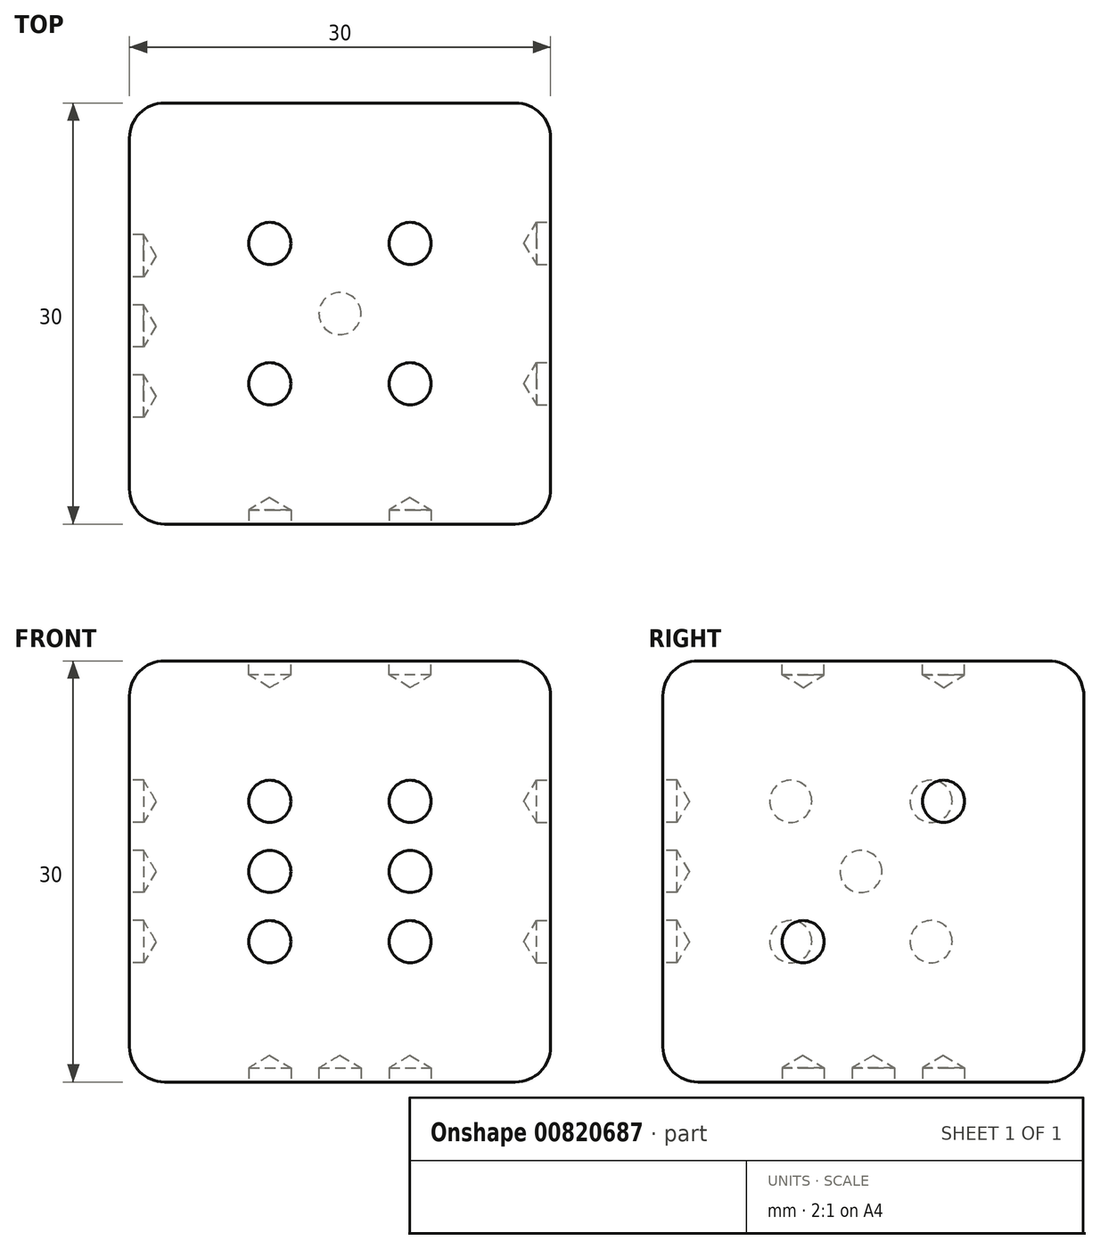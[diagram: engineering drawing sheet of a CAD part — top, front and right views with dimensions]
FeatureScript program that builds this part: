
annotation { "Feature Type Name" : "Feature", "Feature Type Description" : "" }
export const myFeature = defineFeature(function(context is Context, id is Id, definition is map)
    precondition{}
    {
        {
            var Q0;
            Q0=qCreatedBy(makeId("Front.planeOp"),FACE);
            var sketch = newSketch(context, id + "F0", { "sketchPlane" : qUnion([Q0])});
            skLineSegment(sketch, "E0.bottom", {"start": v(15, 15) * mm, "end": v(-15, 15) * mm});
            skLineSegment(sketch, "E0.top", {"start": v(15, -15) * mm, "end": v(-15, -15) * mm});
            skLineSegment(sketch, "E0.left", {"start": v(15, 15) * mm, "end": v(15, -15) * mm});
            skLineSegment(sketch, "E0.right", {"start": v(-15, 15) * mm, "end": v(-15, -15) * mm});
            skPoint(sketch, "E0.middle", {"position": v(0, 0) * mm});
            skSolve(sketch);
        }
        {
            var Q0;
            Q0 = qSketchRegion(id + "F0", true);
            extrude(context, id + "F1", {"entities" : qUnion([Q0]), "depth" : 30 * mm, "offsetDistance" : 25.4 * mm});
        }
        {
            var Q0;
            Q0=makeQuery(id+"F1.opExtrude","CAP_FACE",FACE,{"disambiguationData":[OSD([sQuery(id+"F0.wireOp",EDGE,"E0.bottom"),sQuery(id+"F0.wireOp",EDGE,"E0.top"),sQuery(id+"F0.wireOp",EDGE,"E0.left"),sQuery(id+"F0.wireOp",EDGE,"E0.right")])],"isStart":false});
            var Q1;
            Q1=makeQuery(id+"F1.opExtrude","SWEPT_FACE",FACE,{"disambiguationData":[OSD([sQuery(id+"F0.wireOp",EDGE,"E0.bottom")])]});
            var Q2;
            Q2=makeQuery(id+"F1.opExtrude","SWEPT_FACE",FACE,{"disambiguationData":[OSD([sQuery(id+"F0.wireOp",EDGE,"E0.left")])]});
            var Q3;
            Q3=makeQuery(id+"F1.opExtrude","SWEPT_FACE",FACE,{"disambiguationData":[OSD([sQuery(id+"F0.wireOp",EDGE,"E0.right")])]});
            var Q4;
            Q4=makeQuery(id+"F1.opExtrude","SWEPT_FACE",FACE,{"disambiguationData":[OSD([sQuery(id+"F0.wireOp",EDGE,"E0.top")])]});
            var Q5;
            Q5=makeQuery(id+"F1.opExtrude","CAP_FACE",FACE,{"disambiguationData":[OSD([sQuery(id+"F0.wireOp",EDGE,"E0.bottom"),sQuery(id+"F0.wireOp",EDGE,"E0.top"),sQuery(id+"F0.wireOp",EDGE,"E0.left"),sQuery(id+"F0.wireOp",EDGE,"E0.right")])],"isStart":true});
            fillet(context, id + "F2", {"entities" : qUnion([Q0, Q1, Q2, Q3, Q4, Q5]), "radius" : 2.5 * mm, "tangentPropagation" : true, "allowEdgeOverflow" : false});
        }
        {
            var Q0;
            Q0=makeQuery(id+"F1.opExtrude","CAP_FACE",FACE,{"disambiguationData":[OSD([sQuery(id+"F0.wireOp",EDGE,"E0.bottom"),sQuery(id+"F0.wireOp",EDGE,"E0.top"),sQuery(id+"F0.wireOp",EDGE,"E0.left"),sQuery(id+"F0.wireOp",EDGE,"E0.right")])],"isStart":false});
            var sketch = newSketch(context, id + "F3", { "sketchPlane" : qUnion([Q0])});
            skPoint(sketch, "E1.middle", {"position": v(0, 0) * mm});
            skPoint(sketch, "E2", {"position": v(-5, 0) * mm});
            skPoint(sketch, "E3", {"position": v(-5, 5) * mm});
            skPoint(sketch, "E4", {"position": v(-5, -5) * mm});
            skPoint(sketch, "E5", {"position": v(5, -5) * mm});
            skPoint(sketch, "E6", {"position": v(5, 5) * mm});
            skPoint(sketch, "E7", {"position": v(5, 0) * mm});
            skSolve(sketch);
        }
        {
            var Q0;
            Q0=makeQuery(id+"F1.opExtrude","SWEPT_FACE",FACE,{"disambiguationData":[OSD([sQuery(id+"F0.wireOp",EDGE,"E0.bottom")])]});
            var sketch = newSketch(context, id + "F4", { "sketchPlane" : qUnion([Q0])});
            skPoint(sketch, "E8.middle", {"position": v(0, 0) * mm});
            skPoint(sketch, "E9", {"position": v(-5, -10) * mm});
            skPoint(sketch, "E10", {"position": v(5, -10) * mm});
            skPoint(sketch, "E11", {"position": v(5, -20) * mm});
            skPoint(sketch, "E12", {"position": v(-5, -20) * mm});
            skSolve(sketch);
        }
        {
            var Q0;
            Q0=makeQuery(id+"F1.opExtrude","SWEPT_FACE",FACE,{"disambiguationData":[OSD([sQuery(id+"F0.wireOp",EDGE,"E0.top")])]});
            var sketch = newSketch(context, id + "F5", { "sketchPlane" : qUnion([Q0])});
            skPoint(sketch, "E13.middle", {"position": v(0, 0) * mm});
            skPoint(sketch, "E14", {"position": v(0, 15) * mm});
            skPoint(sketch, "E15", {"position": v(-5, 10) * mm});
            skPoint(sketch, "E16", {"position": v(5, 20) * mm});
            skSolve(sketch);
        }
        {
            var Q0;
            Q0=makeQuery(id+"F1.opExtrude","SWEPT_FACE",FACE,{"disambiguationData":[OSD([sQuery(id+"F0.wireOp",EDGE,"E0.right")])]});
            var sketch = newSketch(context, id + "F6", { "sketchPlane" : qUnion([Q0])});
            skPoint(sketch, "E17.middle", {"position": v(0.88, 0) * mm});
            skPoint(sketch, "E18", {"position": v(15.88, 0) * mm});
            skPoint(sketch, "E19", {"position": v(10.88, 5) * mm});
            skPoint(sketch, "E20", {"position": v(20.88, 5) * mm});
            skPoint(sketch, "E21", {"position": v(20.88, -5) * mm});
            skPoint(sketch, "E22", {"position": v(10.88, -5) * mm});
            skSolve(sketch);
        }
        {
            var Q0;
            Q0=makeQuery(id+"F1.opExtrude","SWEPT_FACE",FACE,{"disambiguationData":[OSD([sQuery(id+"F0.wireOp",EDGE,"E0.left")])]});
            var sketch = newSketch(context, id + "F7", { "sketchPlane" : qUnion([Q0])});
            skPoint(sketch, "E23.middle", {"position": v(0, 0) * mm});
            skPoint(sketch, "E24", {"position": v(-20, -5) * mm});
            skPoint(sketch, "E25", {"position": v(-10, 5) * mm});
            skSolve(sketch);
        }
        {
            var Q0;
            Q0=sQuery(id+"F3.wireOp",VERTEX,"E3");
            var Q1;
            Q1=sQuery(id+"F3.wireOp",VERTEX,"E6");
            var Q2;
            Q2=sQuery(id+"F3.wireOp",VERTEX,"E7");
            var Q3;
            Q3=sQuery(id+"F3.wireOp",VERTEX,"E2");
            var Q4;
            Q4=sQuery(id+"F3.wireOp",VERTEX,"E4");
            var Q5;
            Q5=sQuery(id+"F3.wireOp",VERTEX,"E5");
            var Q6;
            Q6=sQuery(id+"F4.wireOp",VERTEX,"E12");
            var Q7;
            Q7=sQuery(id+"F4.wireOp",VERTEX,"E9");
            var Q8;
            Q8=sQuery(id+"F4.wireOp",VERTEX,"E10");
            var Q9;
            Q9=sQuery(id+"F4.wireOp",VERTEX,"E11");
            var Q10;
            Q10=sQuery(id+"F7.wireOp",VERTEX,"E25");
            var Q11;
            Q11=sQuery(id+"F7.wireOp",VERTEX,"E24");
            var Q12;
            Q12=sQuery(id+"F6.wireOp",VERTEX,"E20");
            var Q13;
            Q13=sQuery(id+"F6.wireOp",VERTEX,"E18");
            var Q14;
            Q14=sQuery(id+"F6.wireOp",VERTEX,"E22");
            var Q15;
            Q15=sQuery(id+"F6.wireOp",VERTEX,"E19");
            var Q16;
            Q16=sQuery(id+"F6.wireOp",VERTEX,"E21");
            var Q17;
            Q17=sQuery(id+"F5.wireOp",VERTEX,"E15");
            var Q18;
            Q18=sQuery(id+"F5.wireOp",VERTEX,"E14");
            var Q19;
            Q19=sQuery(id+"F5.wireOp",VERTEX,"E16");
            var Q20;
            Q20=makeQuery(id+"F1.opExtrude","SWEPT_BODY",BODY,{"disambiguationData":[OSD([sQuery(id+"F0.wireOp",EDGE,"E0.bottom"),sQuery(id+"F0.wireOp",EDGE,"E0.top"),sQuery(id+"F0.wireOp",EDGE,"E0.left"),sQuery(id+"F0.wireOp",EDGE,"E0.right")])]});
            hole(context, id + "F8", {"style" : HoleStyle.SIMPLE, "endStyle" : HoleEndStyle.BLIND, "holeDiameter" : 3 * mm, "majorDiameter" : 6.35 * mm, "holeDepth" : 1 * mm, "isTappedThrough" : true, "tappedDepth" : 12.7 * mm, "tapClearance" : 3, "locations" : qUnion([Q0, Q1, Q2, Q3, Q4, Q5, Q6, Q7, Q8, Q9, Q10, Q11, Q12, Q13, Q14, Q15, Q16, Q17, Q18, Q19]), "scope" : qUnion([Q20])});
        }
    });
